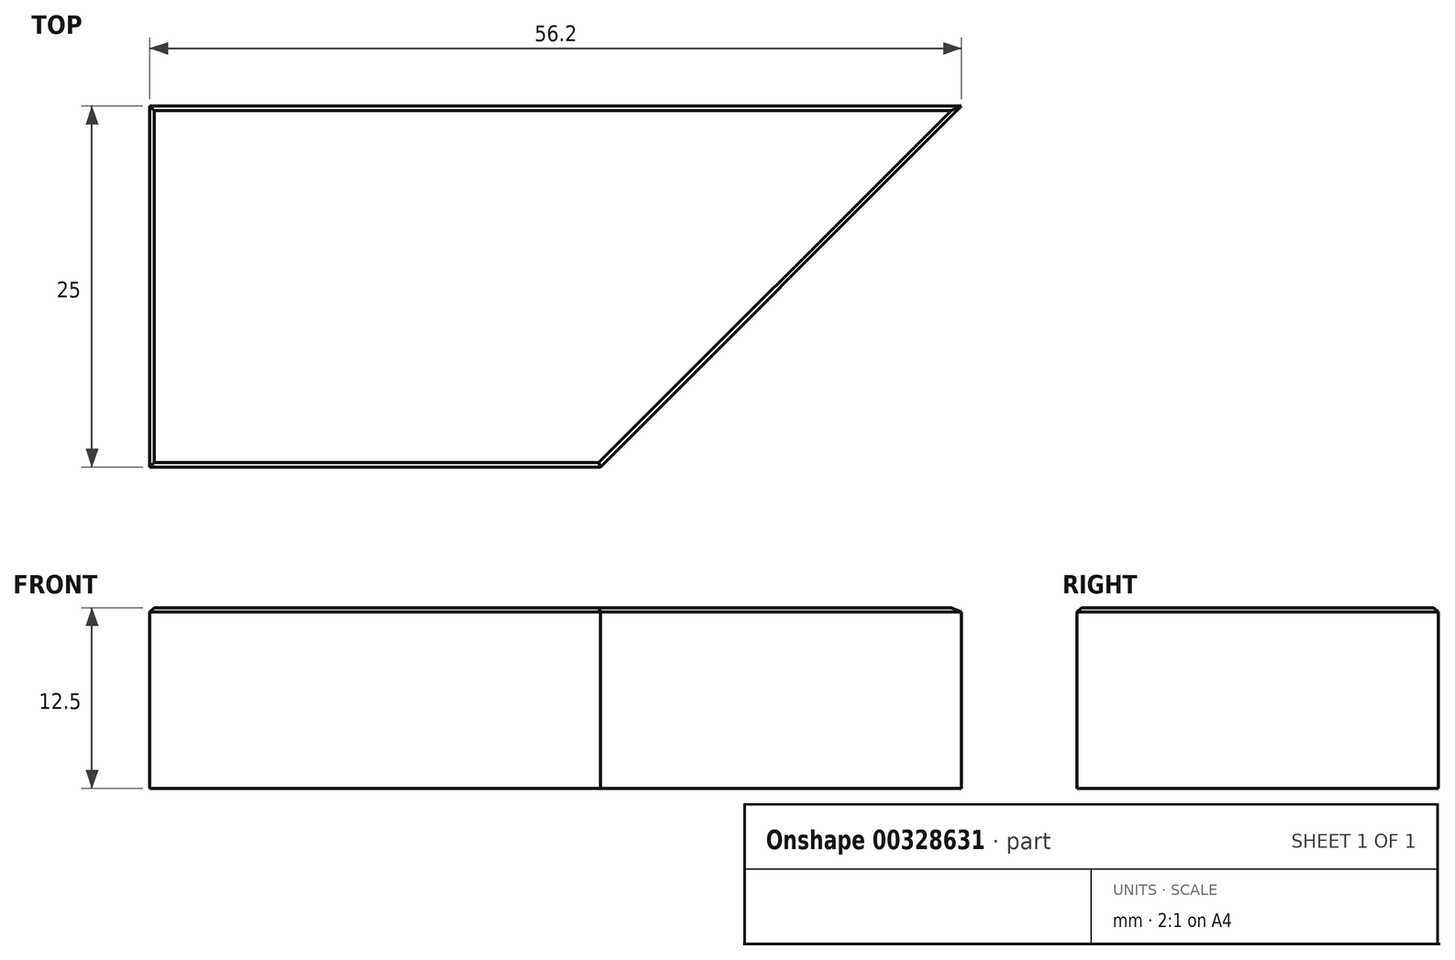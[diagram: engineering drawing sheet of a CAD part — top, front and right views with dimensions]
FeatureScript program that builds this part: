
annotation { "Feature Type Name" : "Feature", "Feature Type Description" : "" }
export const myFeature = defineFeature(function(context is Context, id is Id, definition is map)
    precondition{}
    {
        {
            var Q0;
            Q0=qCreatedBy(makeId("Top.planeOp"),FACE);
            var sketch = newSketch(context, id + "F0", { "sketchPlane" : qUnion([Q0])});
            skLineSegment(sketch, "E0.bottom", {"start": v(56.2, 0) * mm, "end": v(0, 0) * mm});
            skLineSegment(sketch, "E0.top", {"start": v(31.2, -25) * mm, "end": v(0, -25) * mm});
            skLineSegment(sketch, "E0.right", {"start": v(0, 0) * mm, "end": v(0, -25) * mm});
            skPoint(sketch, "E0.middle", {"position": v(0, 0) * mm});
            skLineSegment(sketch, "E1", {"start": v(31.2, -25) * mm, "end": v(56.2, 0) * mm});
            skSolve(sketch);
        }
        {
            var Q0;
            Q0=qSketchRegion(id+"F0",true);
            extrude(context, id + "F1", {"entities" : qUnion([Q0]), "oppositeDirection" : true, "depth" : 12.5 * mm});
        }
        {
            var Q0;
            Q0=makeQuery(id+"F1.opExtrude","CAP_FACE",FACE,{"disambiguationData":[OSD([sQuery(id+"F0.wireOp",EDGE,"E0.bottom"),sQuery(id+"F0.wireOp",EDGE,"E0.top"),sQuery(id+"F0.wireOp",EDGE,"E0.left"),sQuery(id+"F0.wireOp",EDGE,"E0.right")])],"isStart":true});
            chamfer(context, id + "F2", {"entities" : qUnion([Q0]), "width" : .3 * mm, "tangentPropagation" : true});
        }
    });
